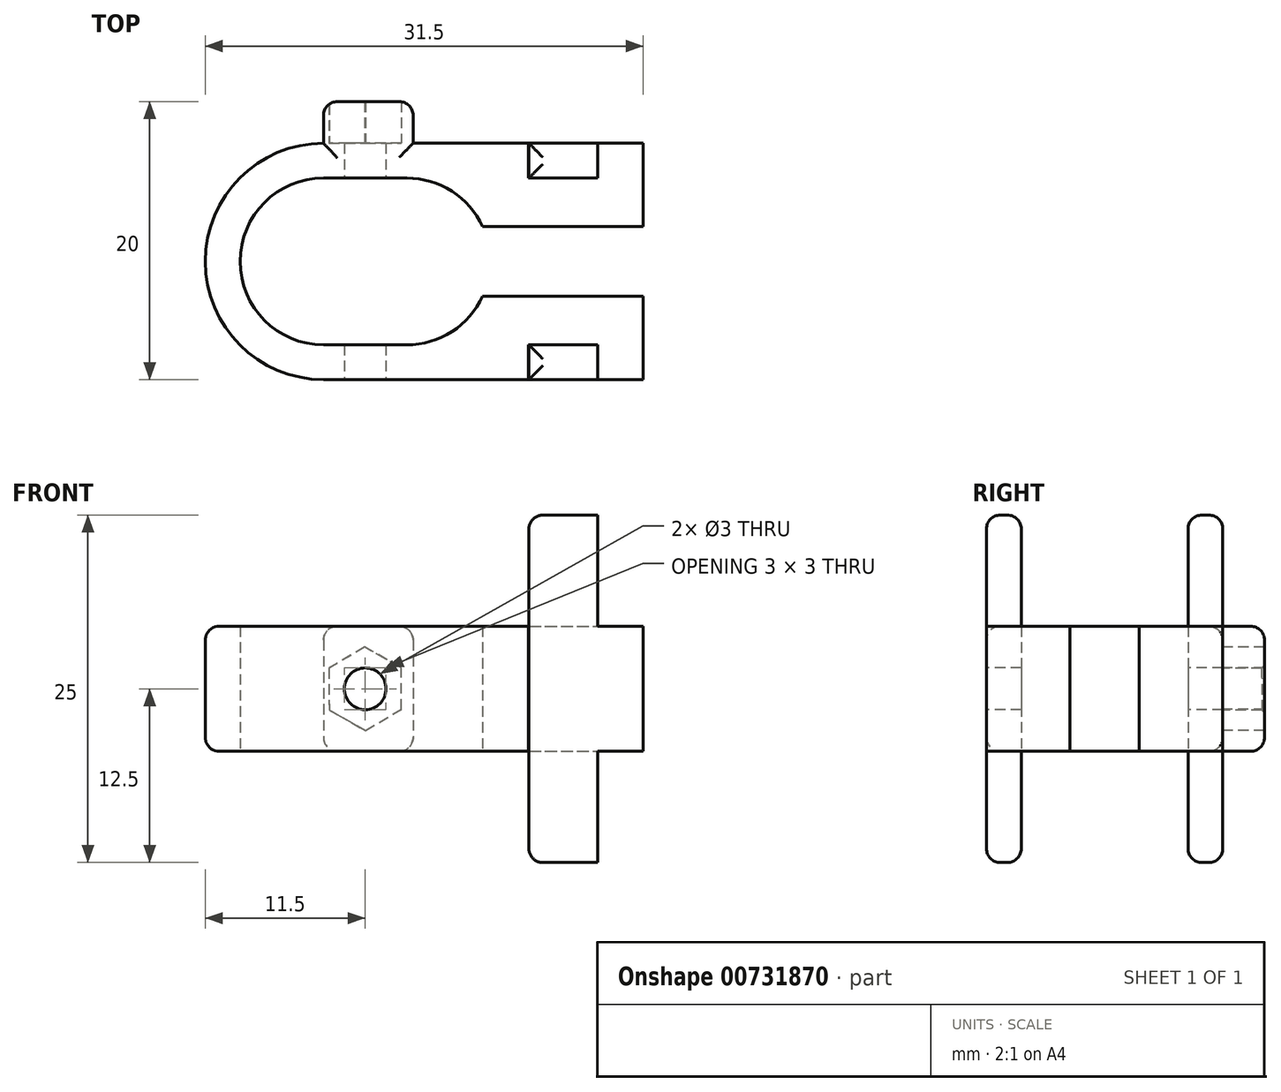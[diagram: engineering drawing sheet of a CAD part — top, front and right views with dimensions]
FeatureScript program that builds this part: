
annotation { "Feature Type Name" : "Feature", "Feature Type Description" : "" }
export const myFeature = defineFeature(function(context is Context, id is Id, definition is map)
    precondition{}
    {
        {
            var Q0;
            Q0=qCreatedBy(makeId("Top.planeOp"),FACE);
            var sketch = newSketch(context, id + "F0", { "sketchPlane" : qUnion([Q0])});
            skLineSegment(sketch, "E0", {"start": v(-23, 0) * mm, "end": v(0, 0) * mm});
            skLineSegment(sketch, "E1", {"start": v(0, 0) * mm, "end": v(0, 6) * mm});
            skLineSegment(sketch, "E2", {"start": v(0, 17) * mm, "end": v(-23, 17) * mm});
            skArc(sketch, "E3", {"start": v(-23, 0) * mm, "mid": v(-31.5, 8.5) * mm, "end": v(-23, 17) * mm});
            skLineSegment(sketch, "E4.0", {"start": v(0, 11) * mm, "end": v(-11.55, 11) * mm});
            skLineSegment(sketch, "E5.trimOffspring", {"start": v(0, 11) * mm, "end": v(0, 17) * mm});
            skArc(sketch, "E6", {"start": v(-23, 14.5) * mm, "mid": v(-29, 8.5) * mm, "end": v(-23, 2.5) * mm});
            skArc(sketch, "E7", {"start": v(-11.55, 11) * mm, "mid": v(-13.76, 13.55) * mm, "end": v(-17, 14.5) * mm});
            skLineSegment(sketch, "E8", {"start": v(-23, 14.5) * mm, "end": v(-17, 14.5) * mm});
            skLineSegment(sketch, "E9", {"start": v(-23, 2.5) * mm, "end": v(-17, 2.5) * mm});
            skLineSegment(sketch, "E10.trimOffspring", {"start": v(-11.55, 6) * mm, "end": v(0, 6) * mm});
            skArc(sketch, "E11.trimOffspring", {"start": v(-17, 2.5) * mm, "mid": v(-13.76, 3.45) * mm, "end": v(-11.55, 6) * mm});
            skLineSegment(sketch, "E12", {"start": v(-5.77, 0) * mm, "end": v(-8.26, 0) * mm});
            skLineSegment(sketch, "E13", {"start": v(-8.26, 0) * mm, "end": v(-8.26, 2.5) * mm});
            skLineSegment(sketch, "E14", {"start": v(-8.26, 2.5) * mm, "end": v(-3.26, 2.5) * mm});
            skLineSegment(sketch, "E15", {"start": v(-3.26, 2.5) * mm, "end": v(-3.26, 0) * mm});
            skLineSegment(sketch, "E16", {"start": v(-3.26, 0) * mm, "end": v(-8.26, 0) * mm});
            skLineSegment(sketch, "E17", {"start": v(-23, 8.5) * mm, "end": v(-17, 8.5) * mm, "construction": true});
            skLineSegment(sketch, "E18.MirrorCS", {"start": v(-8.26, 17) * mm, "end": v(-8.26, 14.5) * mm});
            skLineSegment(sketch, "E19.MirrorCS", {"start": v(-8.26, 14.5) * mm, "end": v(-3.26, 14.5) * mm});
            skLineSegment(sketch, "E20.MirrorCS", {"start": v(-3.26, 14.5) * mm, "end": v(-3.26, 17) * mm});
            skLineSegment(sketch, "E21.MirrorCS", {"start": v(-3.26, 17) * mm, "end": v(-8.26, 17) * mm});
            skSolve(sketch);
        }
        {
            var Q0;
            Q0=qCreatedBy(makeId("Top.planeOp"),FACE);
            var sketch = newSketch(context, id + "F1", { "sketchPlane" : qUnion([Q0])});
            skLineSegment(sketch, "E22.bottom", {"start": v(-3.26, 0) * mm, "end": v(-8.22, 0) * mm});
            skLineSegment(sketch, "E22.top", {"start": v(-3.26, 2.5) * mm, "end": v(-8.22, 2.5) * mm});
            skLineSegment(sketch, "E22.left", {"start": v(-3.26, 0) * mm, "end": v(-3.26, 2.5) * mm});
            skLineSegment(sketch, "E22.right", {"start": v(-8.22, 0) * mm, "end": v(-8.22, 2.5) * mm});
            skLineSegment(sketch, "E23.MirrorCS", {"start": v(-8.22, 17) * mm, "end": v(-8.22, 14.5) * mm});
            skLineSegment(sketch, "E24.MirrorCS", {"start": v(-3.26, 14.5) * mm, "end": v(-8.22, 14.5) * mm});
            skLineSegment(sketch, "E25.MirrorCS", {"start": v(-3.26, 17) * mm, "end": v(-3.26, 14.5) * mm});
            skLineSegment(sketch, "E26.MirrorCS", {"start": v(-3.26, 17) * mm, "end": v(-8.22, 17) * mm});
            skSolve(sketch);
        }
        {
            var Q0;
            {var subQ8=sQuery(id+"F0.wireOp",EDGE,"E1");Q0=makeQuery(id+"F0.imprint","IMPRINT",FACE,{"disambiguationData":[TD([[makeQuery(id+"F0.imprint","IMPRINT",EDGE,{"derivedFrom":subQ8}),1.0]])]});}
            extrude(context, id + "F2", {"entities" : qUnion([Q0]), "depth" : 4.5 * mm, "offsetDistance" : 25 * mm, "hasSecondDirection" : true, "secondDirectionOppositeDirection" : true, "secondDirectionDepth" : 4.5 * mm});
        }
        {
            var Q0;
            Q0=makeQuery(id+"F1.imprint","IMPRINT",FACE,{"disambiguationData":[TD([[makeQuery(id+"F1.imprint","IMPRINT",EDGE,{"derivedFrom":sQuery(id+"F1.wireOp",EDGE,"E22.bottom")}),-1.0]])]});
            var Q1;
            Q1=makeQuery(id+"F1.imprint","IMPRINT",FACE,{"disambiguationData":[TD([[makeQuery(id+"F1.imprint","IMPRINT",EDGE,{"derivedFrom":sQuery(id+"F1.wireOp",EDGE,"E23.MirrorCS")}),1.0]])]});
            extrude(context, id + "F3", {"entities" : qUnion([Q0, Q1]), "operationType" : NewBodyOperationType.ADD, "depth" : 12.5 * mm, "offsetDistance" : 25 * mm, "hasSecondDirection" : true, "secondDirectionOppositeDirection" : true, "secondDirectionDepth" : 12.5 * mm});
        }
        {
            var Q0;
            {var subQ0=sQuery(id+"F0.wireOp",EDGE,"E0");Q0=makeQuery(id+"F2.opExtrude","SWEPT_FACE",FACE,{"disambiguationData":[OSD([subQ0]),TDD([makeQuery(id+"F0.imprint","IMPRINT",EDGE,{"disambiguationData":[TD([[makeQuery(id+"F0.imprint","INTERSECT",VERTEX,{"derivedFrom":[subQ0,sQuery(id+"F0.wireOp",EDGE,"E3")]}),-1.0]])],"derivedFrom":subQ0})])]});}
            var sketch = newSketch(context, id + "F4", { "sketchPlane" : qUnion([Q0])});
            skCircle(sketch, "E27", {"center": v(-20, 0) * mm, "radius": 1.5 * mm});
            skPoint(sketch, "E27.centerSnap0", {"position": v(-23, 0) * mm});
            skSolve(sketch);
        }
        {
            var Q0;
            Q0=makeQuery(id+"F4.imprint","IMPRINT",FACE,{"disambiguationData":[TD([[makeQuery(id+"F4.imprint","IMPRINT",EDGE,{"derivedFrom":sQuery(id+"F4.wireOp",EDGE,"E27")}),1.0]])]});
            extrude(context, id + "F5", {"entities" : qUnion([Q0]), "operationType" : NewBodyOperationType.REMOVE, "endBound" : BoundingType.THROUGH_ALL, "oppositeDirection" : true, "depth" : 25 * mm, "offsetDistance" : 25 * mm});
        }
        {
            var Q0;
            {var subQ0=sQuery(id+"F0.wireOp",EDGE,"E2");Q0=makeQuery(id+"F2.opExtrude","SWEPT_FACE",FACE,{"disambiguationData":[OSD([subQ0]),TDD([makeQuery(id+"F0.imprint","IMPRINT",EDGE,{"disambiguationData":[TD([[makeQuery(id+"F0.imprint","INTERSECT",VERTEX,{"derivedFrom":[subQ0,sQuery(id+"F0.wireOp",EDGE,"E3")]}),1.0]])],"derivedFrom":subQ0})])]});}
            var sketch = newSketch(context, id + "F6", { "sketchPlane" : qUnion([Q0])});
            skCircle(sketch, "E28.cCircle", {"center": v(20, 0) * mm, "radius": 2.6 * mm, "construction": true});
            skLineSegment(sketch, "E28.0", {"start": v(19.98, -3) * mm, "end": v(17.4, -1.48) * mm});
            skLineSegment(sketch, "E28.1", {"start": v(17.4, -1.48) * mm, "end": v(17.41, 1.52) * mm});
            skLineSegment(sketch, "E28.2", {"start": v(17.41, 1.52) * mm, "end": v(20.02, 3) * mm});
            skLineSegment(sketch, "E28.3", {"start": v(20.02, 3) * mm, "end": v(22.6, 1.48) * mm});
            skLineSegment(sketch, "E28.4", {"start": v(22.6, 1.48) * mm, "end": v(22.59, -1.52) * mm});
            skLineSegment(sketch, "E28.5", {"start": v(22.59, -1.52) * mm, "end": v(19.98, -3) * mm});
            skPoint(sketch, "E28.0.midPoint", {"position": v(18.68, -2.24) * mm});
            skLineSegment(sketch, "E29.bottom", {"start": v(23, 4.5) * mm, "end": v(16.55, 4.5) * mm});
            skLineSegment(sketch, "E29.top", {"start": v(23, -4.5) * mm, "end": v(16.55, -4.5) * mm});
            skLineSegment(sketch, "E29.left", {"start": v(23, 4.5) * mm, "end": v(23, -4.5) * mm});
            skLineSegment(sketch, "E29.right", {"start": v(16.55, 4.5) * mm, "end": v(16.55, -4.5) * mm});
            skSolve(sketch);
        }
        {
            var Q0;
            Q0 = qSketchRegion(id + "F6", true);
            extrude(context, id + "F7", {"entities" : qUnion([Q0]), "operationType" : NewBodyOperationType.ADD, "depth" : 3 * mm, "offsetDistance" : 25 * mm});
        }
        {
            var Q0;
            Q0=makeQuery(id+"F3.opExtrude","CAP_EDGE",EDGE,{"disambiguationData":[OSD([sQuery(id+"F1.wireOp",EDGE,"E22.top")])],"isStart":true});
            var Q1;
            Q1=makeQuery(id+"F3.opExtrude","CAP_EDGE",EDGE,{"disambiguationData":[OSD([sQuery(id+"F1.wireOp",EDGE,"E22.right")])],"isStart":true});
            var Q2;
            Q2=makeQuery(id+"F3.opExtrude","CAP_EDGE",EDGE,{"disambiguationData":[OSD([sQuery(id+"F1.wireOp",EDGE,"E24.MirrorCS")])],"isStart":true});
            var Q3;
            Q3=makeQuery(id+"F3.opExtrude","CAP_EDGE",EDGE,{"disambiguationData":[OSD([sQuery(id+"F1.wireOp",EDGE,"E23.MirrorCS")])],"isStart":true});
            var Q4;
            Q4=makeQuery(id+"F3.opExtrude","CAP_EDGE",EDGE,{"disambiguationData":[OSD([sQuery(id+"F1.wireOp",EDGE,"E26.MirrorCS")])],"isStart":true});
            var Q5;
            Q5=makeQuery(id+"F3.opExtrude","CAP_EDGE",EDGE,{"disambiguationData":[OSD([sQuery(id+"F1.wireOp",EDGE,"E22.bottom")])],"isStart":true});
            var Q6;
            Q6=makeQuery(id+"F3.opExtrude","CAP_EDGE",EDGE,{"disambiguationData":[OSD([sQuery(id+"F1.wireOp",EDGE,"E22.bottom")])],"isStart":false});
            var Q7;
            Q7=makeQuery(id+"F3.opExtrude","CAP_EDGE",EDGE,{"disambiguationData":[OSD([sQuery(id+"F1.wireOp",EDGE,"E22.right")])],"isStart":false});
            var Q8;
            Q8=makeQuery(id+"F3.opExtrude","CAP_EDGE",EDGE,{"disambiguationData":[OSD([sQuery(id+"F1.wireOp",EDGE,"E22.top")])],"isStart":false});
            var Q9;
            Q9=makeQuery(id+"F3.opExtrude","CAP_EDGE",EDGE,{"disambiguationData":[OSD([sQuery(id+"F1.wireOp",EDGE,"E24.MirrorCS")])],"isStart":false});
            var Q10;
            Q10=makeQuery(id+"F3.opExtrude","CAP_EDGE",EDGE,{"disambiguationData":[OSD([sQuery(id+"F1.wireOp",EDGE,"E23.MirrorCS")])],"isStart":false});
            var Q11;
            Q11=makeQuery(id+"F3.opExtrude","CAP_EDGE",EDGE,{"disambiguationData":[OSD([sQuery(id+"F1.wireOp",EDGE,"E26.MirrorCS")])],"isStart":false});
            var Q12;
            {var subQ0=sQuery(id+"F0.wireOp",EDGE,"E0");Q12=makeQuery(id+"F2.opExtrude","CAP_EDGE",EDGE,{"disambiguationData":[OSD([subQ0]),TDD([makeQuery(id+"F0.imprint","IMPRINT",EDGE,{"disambiguationData":[TD([[makeQuery(id+"F0.imprint","INTERSECT",VERTEX,{"derivedFrom":[subQ0,sQuery(id+"F0.wireOp",EDGE,"E3")]}),-1.0]])],"derivedFrom":subQ0})])],"isStart":true});}
            var Q13;
            Q13=makeQuery(id+"F2.opExtrude","CAP_EDGE",EDGE,{"disambiguationData":[OSD([sQuery(id+"F0.wireOp",EDGE,"E3")])],"isStart":true});
            var Q14;
            Q14=makeQuery(id+"F7.opExtrude","SWEPT_EDGE",EDGE,{"disambiguationData":[OSD([sQuery(id+"F6.wireOp",EDGE,"E29.top"),sQuery(id+"F6.wireOp",EDGE,"E29.left")])]});
            var Q15;
            Q15=makeQuery(id+"F7.opExtrude","CAP_EDGE",EDGE,{"disambiguationData":[OSD([sQuery(id+"F6.wireOp",EDGE,"E29.top")])],"isStart":false});
            var Q16;
            Q16=makeQuery(id+"F7.opExtrude","SWEPT_EDGE",EDGE,{"disambiguationData":[OSD([sQuery(id+"F0.wireOp",EDGE,"E2"),sQuery(id+"F6.wireOp",EDGE,"E29.top"),sQuery(id+"F6.wireOp",EDGE,"E29.right")])]});
            var Q17;
            {var subQ0=sQuery(id+"F0.wireOp",EDGE,"E2");Q17=makeQuery(id+"F2.opExtrude","CAP_EDGE",EDGE,{"disambiguationData":[OSD([subQ0]),TDD([makeQuery(id+"F0.imprint","IMPRINT",EDGE,{"disambiguationData":[TD([[makeQuery(id+"F0.imprint","INTERSECT",VERTEX,{"derivedFrom":[subQ0,sQuery(id+"F0.wireOp",EDGE,"E3")]}),1.0]])],"derivedFrom":subQ0})])],"isStart":true});}
            var Q18;
            {var subQ0=sQuery(id+"F0.wireOp",EDGE,"E2");Q18=makeQuery(id+"F2.opExtrude","CAP_EDGE",EDGE,{"disambiguationData":[OSD([subQ0]),TDD([makeQuery(id+"F0.imprint","IMPRINT",EDGE,{"disambiguationData":[TD([[makeQuery(id+"F0.imprint","INTERSECT",VERTEX,{"derivedFrom":[subQ0,sQuery(id+"F0.wireOp",EDGE,"E3")]}),1.0]])],"derivedFrom":subQ0})])],"isStart":false});}
            var Q19;
            Q19=makeQuery(id+"F7.opExtrude","SWEPT_EDGE",EDGE,{"disambiguationData":[OSD([sQuery(id+"F0.wireOp",EDGE,"E2"),sQuery(id+"F6.wireOp",EDGE,"E29.bottom"),sQuery(id+"F6.wireOp",EDGE,"E29.right")])]});
            var Q20;
            Q20=makeQuery(id+"F7.opExtrude","CAP_EDGE",EDGE,{"disambiguationData":[OSD([sQuery(id+"F6.wireOp",EDGE,"E29.bottom")])],"isStart":false});
            var Q21;
            Q21=makeQuery(id+"F7.opExtrude","SWEPT_EDGE",EDGE,{"disambiguationData":[OSD([sQuery(id+"F6.wireOp",EDGE,"E29.bottom"),sQuery(id+"F6.wireOp",EDGE,"E29.left")])]});
            var Q22;
            Q22=makeQuery(id+"F2.opExtrude","CAP_EDGE",EDGE,{"disambiguationData":[OSD([sQuery(id+"F0.wireOp",EDGE,"E3")])],"isStart":false});
            var Q23;
            {var subQ0=sQuery(id+"F0.wireOp",EDGE,"E0");Q23=makeQuery(id+"F2.opExtrude","CAP_EDGE",EDGE,{"disambiguationData":[OSD([subQ0]),TDD([makeQuery(id+"F0.imprint","IMPRINT",EDGE,{"disambiguationData":[TD([[makeQuery(id+"F0.imprint","INTERSECT",VERTEX,{"derivedFrom":[subQ0,sQuery(id+"F0.wireOp",EDGE,"E3")]}),-1.0]])],"derivedFrom":subQ0})])],"isStart":false});}
            var Q24;
            Q24=makeQuery(id+"F7.opExtrude","CAP_EDGE",EDGE,{"disambiguationData":[OSD([sQuery(id+"F6.wireOp",EDGE,"E29.left")])],"isStart":false});
            var Q25;
            Q25=makeQuery(id+"F7.opExtrude","CAP_EDGE",EDGE,{"disambiguationData":[OSD([sQuery(id+"F6.wireOp",EDGE,"E29.right")])],"isStart":false});
            fillet(context, id + "F8", {"entities" : qUnion([Q0, Q1, Q2, Q3, Q4, Q5, Q6, Q7, Q8, Q9, Q10, Q11, Q12, Q13, Q14, Q15, Q16, Q17, Q18, Q19, Q20, Q21, Q22, Q23, Q24, Q25]), "radius" : 1 * mm, "tangentPropagation" : true, "allowEdgeOverflow" : false});
        }
    });
